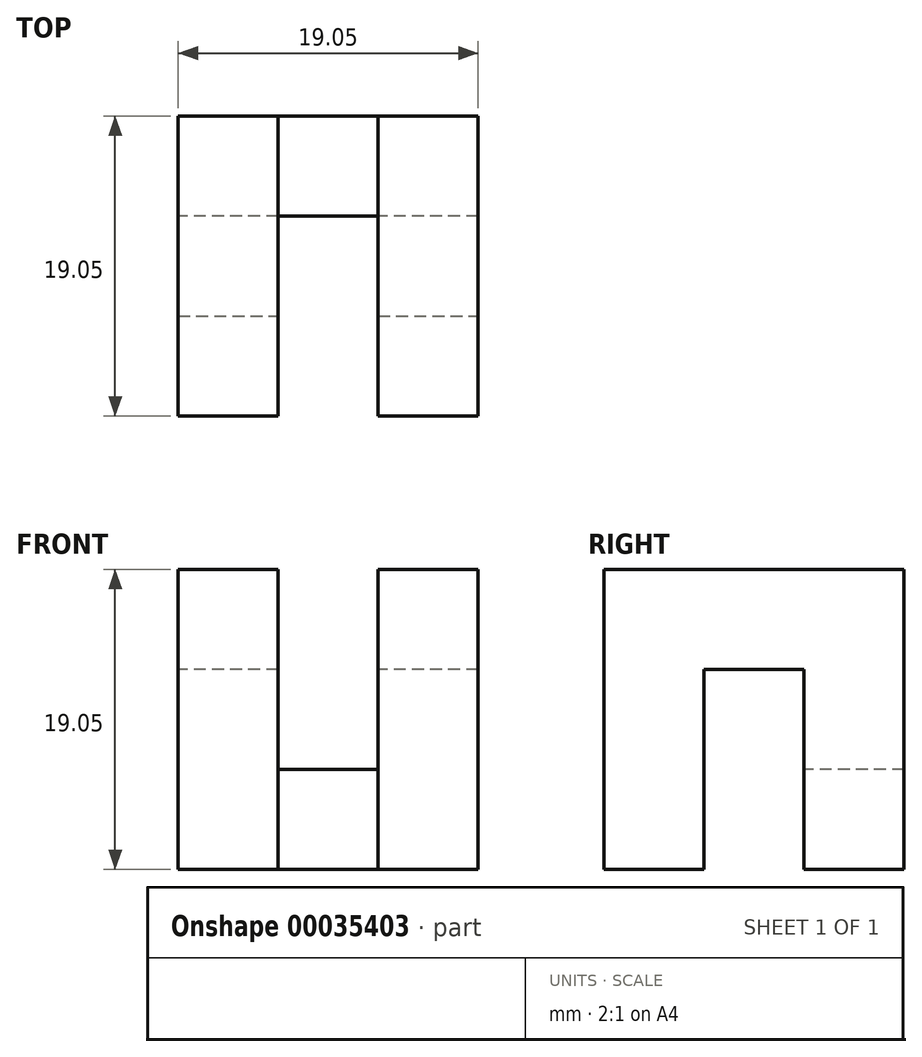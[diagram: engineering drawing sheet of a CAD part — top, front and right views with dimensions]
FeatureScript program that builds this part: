
annotation { "Feature Type Name" : "Feature", "Feature Type Description" : "" }
export const myFeature = defineFeature(function(context is Context, id is Id, definition is map)
    precondition{}
    {
        {
            var Q0;
            Q0=qCreatedBy(makeId("Top.planeOp"),FACE);
            var sketch = newSketch(context, id + "F0", { "sketchPlane" : qUnion([Q0])});
            skLineSegment(sketch, "E0.bottom", {"start": v(0, 0) * mm, "end": v(6.35, 0) * mm});
            skLineSegment(sketch, "E0.top", {"start": v(0, 6.35) * mm, "end": v(6.35, 6.35) * mm});
            skLineSegment(sketch, "E0.left", {"start": v(0, 0) * mm, "end": v(0, 6.35) * mm});
            skLineSegment(sketch, "E0.right", {"start": v(6.35, 0) * mm, "end": v(6.35, 6.35) * mm});
            skSolve(sketch);
        }
        {
            var Q0;
            Q0=makeQuery(id+"F0.imprint","IMPRINT",FACE,{"disambiguationData":[TD([[makeQuery(id+"F0.imprint","IMPRINT",EDGE,{"derivedFrom":sQuery(id+"F0.wireOp",EDGE,"E0.bottom")}),1.0]])]});
            extrude(context, id + "F1", {"entities" : qUnion([Q0]), "depth" : 19.05 * mm});
        }
        {
            var Q0;
            Q0=makeQuery(id+"F1.opExtrude","SWEPT_FACE",FACE,{"disambiguationData":[OSD([sQuery(id+"F0.wireOp",EDGE,"E0.bottom")])]});
            var sketch = newSketch(context, id + "F2", { "sketchPlane" : qUnion([Q0])});
            skLineSegment(sketch, "E1.bottom", {"start": v(6.35, 19.05) * mm, "end": v(0, 19.05) * mm});
            skLineSegment(sketch, "E1.top", {"start": v(6.35, 12.7) * mm, "end": v(0, 12.7) * mm});
            skLineSegment(sketch, "E1.left", {"start": v(6.35, 19.05) * mm, "end": v(6.35, 12.7) * mm});
            skLineSegment(sketch, "E1.right", {"start": v(0, 19.05) * mm, "end": v(0, 12.7) * mm});
            skSolve(sketch);
        }
        {
            var Q0;
            Q0=makeQuery(id+"F2.imprint","IMPRINT",FACE,{"disambiguationData":[TD([[makeQuery(id+"F2.imprint","IMPRINT",EDGE,{"derivedFrom":sQuery(id+"F2.wireOp",EDGE,"E1.bottom")}),-1.0]])]});
            extrude(context, id + "F3", {"entities" : qUnion([Q0]), "operationType" : NewBodyOperationType.ADD, "oppositeDirection" : true, "depth" : 19.05 * mm});
        }
        {
            var Q0;
            Q0=makeQuery(id+"F3.boolean.opBoolean","MERGE",FACE,{"derivedFrom":[makeQuery(id+"F1.opExtrude","CAP_FACE",FACE,{"disambiguationData":[OSD([sQuery(id+"F0.wireOp",EDGE,"E0.bottom"),sQuery(id+"F0.wireOp",EDGE,"E0.top"),sQuery(id+"F0.wireOp",EDGE,"E0.left"),sQuery(id+"F0.wireOp",EDGE,"E0.right")])],"isStart":false}),makeQuery(id+"F3.opExtrude","SWEPT_FACE",FACE,{"disambiguationData":[OSD([sQuery(id+"F2.wireOp",EDGE,"E1.bottom")])]})]});
            var sketch = newSketch(context, id + "F4", { "sketchPlane" : qUnion([Q0])});
            skLineSegment(sketch, "E2.bottom", {"start": v(6.35, 19.05) * mm, "end": v(0, 19.05) * mm});
            skLineSegment(sketch, "E2.top", {"start": v(6.35, 12.7) * mm, "end": v(0, 12.7) * mm});
            skLineSegment(sketch, "E2.left", {"start": v(6.35, 19.05) * mm, "end": v(6.35, 12.7) * mm});
            skLineSegment(sketch, "E2.right", {"start": v(0, 19.05) * mm, "end": v(0, 12.7) * mm});
            skSolve(sketch);
        }
        {
            var Q0;
            Q0=makeQuery(id+"F4.imprint","IMPRINT",FACE,{"disambiguationData":[TD([[makeQuery(id+"F4.imprint","IMPRINT",EDGE,{"derivedFrom":sQuery(id+"F4.wireOp",EDGE,"E2.bottom")}),-1.0]])]});
            extrude(context, id + "F5", {"entities" : qUnion([Q0]), "operationType" : NewBodyOperationType.ADD, "oppositeDirection" : true, "depth" : 19.05 * mm});
        }
        {
            var Q0;
            Q0=makeQuery(id+"F5.boolean.opBoolean","MERGE",FACE,{"derivedFrom":[makeQuery(id+"F3.boolean.opBoolean","MERGE",FACE,{"derivedFrom":[makeQuery(id+"F1.opExtrude","SWEPT_FACE",FACE,{"disambiguationData":[OSD([sQuery(id+"F0.wireOp",EDGE,"E0.left")])]}),makeQuery(id+"F3.opExtrude","SWEPT_FACE",FACE,{"disambiguationData":[OSD([sQuery(id+"F2.wireOp",EDGE,"E1.right")])]})]}),makeQuery(id+"F5.opExtrude","SWEPT_FACE",FACE,{"disambiguationData":[OSD([sQuery(id+"F4.wireOp",EDGE,"E2.right")])]})]});
            var sketch = newSketch(context, id + "F6", { "sketchPlane" : qUnion([Q0])});
            skLineSegment(sketch, "E3.bottom", {"start": v(-19.05, 0) * mm, "end": v(-12.7, 0) * mm});
            skLineSegment(sketch, "E3.top", {"start": v(-19.05, 6.35) * mm, "end": v(-12.7, 6.35) * mm});
            skLineSegment(sketch, "E3.left", {"start": v(-19.05, 0) * mm, "end": v(-19.05, 6.35) * mm});
            skLineSegment(sketch, "E3.right", {"start": v(-12.7, 0) * mm, "end": v(-12.7, 6.35) * mm});
            skSolve(sketch);
        }
        {
            var Q0;
            Q0=makeQuery(id+"F6.imprint","IMPRINT",FACE,{"disambiguationData":[TD([[makeQuery(id+"F6.imprint","IMPRINT",EDGE,{"derivedFrom":sQuery(id+"F6.wireOp",EDGE,"E3.bottom")}),-1.0]])]});
            extrude(context, id + "F7", {"entities" : qUnion([Q0]), "operationType" : NewBodyOperationType.ADD, "oppositeDirection" : true, "depth" : 19.05 * mm});
        }
        {
            var Q0;
            Q0=makeQuery(id+"F7.boolean.opBoolean","MERGE",FACE,{"derivedFrom":[makeQuery(id+"F5.opExtrude","CAP_FACE",FACE,{"disambiguationData":[OSD([sQuery(id+"F4.wireOp",EDGE,"E2.bottom"),sQuery(id+"F4.wireOp",EDGE,"E2.top"),sQuery(id+"F4.wireOp",EDGE,"E2.left"),sQuery(id+"F4.wireOp",EDGE,"E2.right")])],"isStart":false}),makeQuery(id+"F7.opExtrude","SWEPT_FACE",FACE,{"disambiguationData":[OSD([sQuery(id+"F6.wireOp",EDGE,"E3.bottom")])]})]});
            var sketch = newSketch(context, id + "F8", { "sketchPlane" : qUnion([Q0])});
            skLineSegment(sketch, "E4.bottom", {"start": v(19.05, -12.7) * mm, "end": v(12.7, -12.7) * mm});
            skLineSegment(sketch, "E4.top", {"start": v(19.05, -19.05) * mm, "end": v(12.7, -19.05) * mm});
            skLineSegment(sketch, "E4.left", {"start": v(19.05, -12.7) * mm, "end": v(19.05, -19.05) * mm});
            skLineSegment(sketch, "E4.right", {"start": v(12.7, -12.7) * mm, "end": v(12.7, -19.05) * mm});
            skSolve(sketch);
        }
        {
            var Q0;
            Q0=makeQuery(id+"F8.imprint","IMPRINT",FACE,{"disambiguationData":[TD([[makeQuery(id+"F8.imprint","IMPRINT",EDGE,{"derivedFrom":sQuery(id+"F8.wireOp",EDGE,"E4.bottom")}),1.0]])]});
            extrude(context, id + "F9", {"entities" : qUnion([Q0]), "operationType" : NewBodyOperationType.ADD, "oppositeDirection" : true, "depth" : 19.05 * mm});
        }
        {
            var Q0;
            Q0=makeQuery(id+"F9.boolean.opBoolean","MERGE",FACE,{"derivedFrom":[makeQuery(id+"F7.boolean.opBoolean","MERGE",FACE,{"derivedFrom":[makeQuery(id+"F5.boolean.opBoolean","MERGE",FACE,{"derivedFrom":[makeQuery(id+"F3.opExtrude","CAP_FACE",FACE,{"disambiguationData":[OSD([sQuery(id+"F2.wireOp",EDGE,"E1.bottom"),sQuery(id+"F2.wireOp",EDGE,"E1.top"),sQuery(id+"F2.wireOp",EDGE,"E1.left"),sQuery(id+"F2.wireOp",EDGE,"E1.right")])],"isStart":false}),makeQuery(id+"F5.opExtrude","SWEPT_FACE",FACE,{"disambiguationData":[OSD([sQuery(id+"F4.wireOp",EDGE,"E2.bottom")])]})]}),makeQuery(id+"F7.opExtrude","SWEPT_FACE",FACE,{"disambiguationData":[OSD([sQuery(id+"F6.wireOp",EDGE,"E3.left")])]})]}),makeQuery(id+"F9.opExtrude","SWEPT_FACE",FACE,{"disambiguationData":[OSD([sQuery(id+"F8.wireOp",EDGE,"E4.top")])]})]});
            var sketch = newSketch(context, id + "F10", { "sketchPlane" : qUnion([Q0])});
            skLineSegment(sketch, "E5.bottom", {"start": v(-19.05, 19.05) * mm, "end": v(-12.7, 19.05) * mm});
            skLineSegment(sketch, "E5.top", {"start": v(-19.05, 12.7) * mm, "end": v(-12.7, 12.7) * mm});
            skLineSegment(sketch, "E5.left", {"start": v(-19.05, 19.05) * mm, "end": v(-19.05, 12.7) * mm});
            skLineSegment(sketch, "E5.right", {"start": v(-12.7, 19.05) * mm, "end": v(-12.7, 12.7) * mm});
            skSolve(sketch);
        }
        {
            var Q0;
            Q0=makeQuery(id+"F10.imprint","IMPRINT",FACE,{"disambiguationData":[TD([[makeQuery(id+"F10.imprint","IMPRINT",EDGE,{"derivedFrom":sQuery(id+"F10.wireOp",EDGE,"E5.bottom")}),1.0]])]});
            extrude(context, id + "F11", {"entities" : qUnion([Q0]), "operationType" : NewBodyOperationType.ADD, "oppositeDirection" : true, "depth" : 19.05 * mm});
        }
        {
            var Q0;
            Q0=makeQuery(id+"F11.boolean.opBoolean","MERGE",FACE,{"derivedFrom":[makeQuery(id+"F9.opExtrude","CAP_FACE",FACE,{"disambiguationData":[OSD([sQuery(id+"F8.wireOp",EDGE,"E4.bottom"),sQuery(id+"F8.wireOp",EDGE,"E4.top"),sQuery(id+"F8.wireOp",EDGE,"E4.left"),sQuery(id+"F8.wireOp",EDGE,"E4.right")])],"isStart":false}),makeQuery(id+"F11.opExtrude","SWEPT_FACE",FACE,{"disambiguationData":[OSD([sQuery(id+"F10.wireOp",EDGE,"E5.bottom")])]})]});
            var sketch = newSketch(context, id + "F12", { "sketchPlane" : qUnion([Q0])});
            skLineSegment(sketch, "E6.bottom", {"start": v(19.05, 0) * mm, "end": v(12.7, 0) * mm});
            skLineSegment(sketch, "E6.top", {"start": v(19.05, 6.35) * mm, "end": v(12.7, 6.35) * mm});
            skLineSegment(sketch, "E6.left", {"start": v(19.05, 0) * mm, "end": v(19.05, 6.35) * mm});
            skLineSegment(sketch, "E6.right", {"start": v(12.7, 0) * mm, "end": v(12.7, 6.35) * mm});
            skSolve(sketch);
        }
        {
            var Q0;
            Q0=makeQuery(id+"F12.imprint","IMPRINT",FACE,{"disambiguationData":[TD([[makeQuery(id+"F12.imprint","IMPRINT",EDGE,{"derivedFrom":sQuery(id+"F12.wireOp",EDGE,"E6.bottom")}),1.0]])]});
            extrude(context, id + "F13", {"entities" : qUnion([Q0]), "operationType" : NewBodyOperationType.ADD, "oppositeDirection" : true, "depth" : 19.05 * mm});
        }
    });
